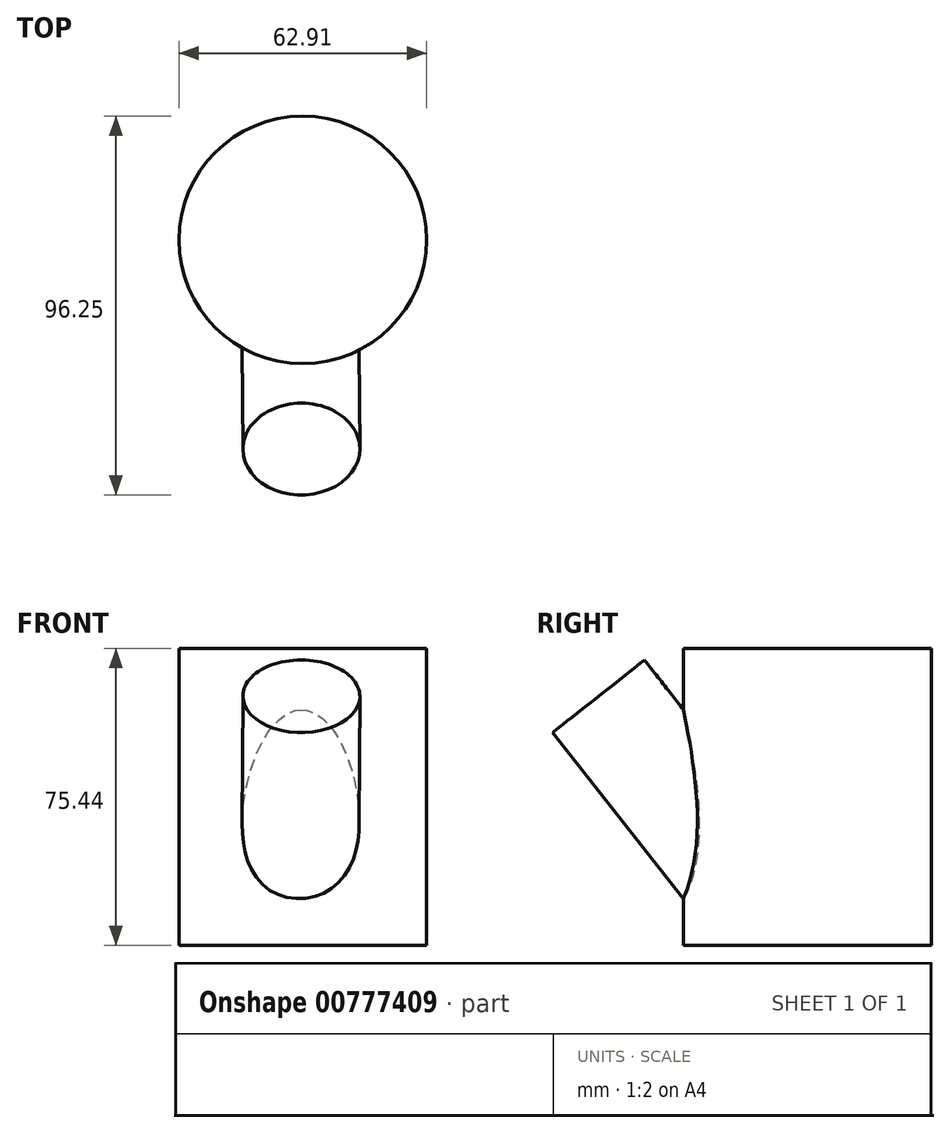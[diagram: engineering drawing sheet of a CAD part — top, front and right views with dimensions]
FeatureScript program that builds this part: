
annotation { "Feature Type Name" : "Feature", "Feature Type Description" : "" }
export const myFeature = defineFeature(function(context is Context, id is Id, definition is map)
    precondition{}
    {
        {
            var Q0;
            Q0=qCreatedBy(makeId("Top.planeOp"),FACE);
            var sketch = newSketch(context, id + "F0", { "sketchPlane" : qUnion([Q0])});
            skCircle(sketch, "E0", {"center": v(-33.12, 24.76) * mm, "radius": 31.45 * mm});
            skPoint(sketch, "E1", {"position": v(-31.15, -6.63) * mm});
            skSolve(sketch);
        }
        {
            var Q0;
            Q0 = qSketchRegion(id + "F0", true);
            extrude(context, id + "F1", {"entities" : qUnion([Q0]), "depth" : 75.44 * mm, "offsetDistance" : 25.4 * mm});
        }
        {
            var Q0;
            Q0=qCreatedBy(makeId("Top.planeOp"),FACE);
            var sketch = newSketch(context, id + "F2", { "sketchPlane" : qUnion([Q0])});
            skPoint(sketch, "E2", {"position": v(24.74, -60.16) * mm});
            skPoint(sketch, "E3", {"position": v(-61.04, -60.73) * mm});
            skSolve(sketch);
        }
        {
            var Q0;
            Q0=qCreatedBy(makeId("Front.planeOp"),FACE);
            var sketch = newSketch(context, id + "F3", { "sketchPlane" : qUnion([Q0])});
            skPoint(sketch, "E4", {"position": v(-36.27, 47.84) * mm});
            skSolve(sketch);
        }
        {
            var Q0;
            Q0=sQuery(id+"F3.wireOp",VERTEX,"E4");
            var Q1;
            Q1=sQuery(id+"F2.wireOp",VERTEX,"E3");
            var Q2;
            Q2=sQuery(id+"F2.wireOp",VERTEX,"E2");
            cPlane(context, id + "F4", {"entities" : qUnion([Q0, Q1, Q2]), "cplaneType" : CPlaneType.THREE_POINT, "offset" : 25.4 * mm, "width" : 152.4 * mm, "height" : 152.4 * mm});
        }
        {
            var Q0;
            Q0=qCreatedBy(id+"F4.planeOp",FACE);
            var sketch = newSketch(context, id + "F5", { "sketchPlane" : qUnion([Q0])});
            skCircle(sketch, "E5", {"center": v(-33.74, -16.97) * mm, "radius": 14.87 * mm});
            skSolve(sketch);
        }
        {
            var Q0;
            Q0=makeQuery(id+"F5.imprint","IMPRINT",FACE,{"disambiguationData":[TD([[makeQuery(id+"F5.imprint","IMPRINT",EDGE,{"derivedFrom":sQuery(id+"F5.wireOp",EDGE,"E5")}),1.0]])]});
            extrude(context, id + "F6", {"entities" : qUnion([Q0]), "operationType" : NewBodyOperationType.ADD, "endBound" : BoundingType.SYMMETRIC, "oppositeDirection" : true, "depth" : 59.44 * mm, "offsetDistance" : 25.4 * mm});
        }
    });
